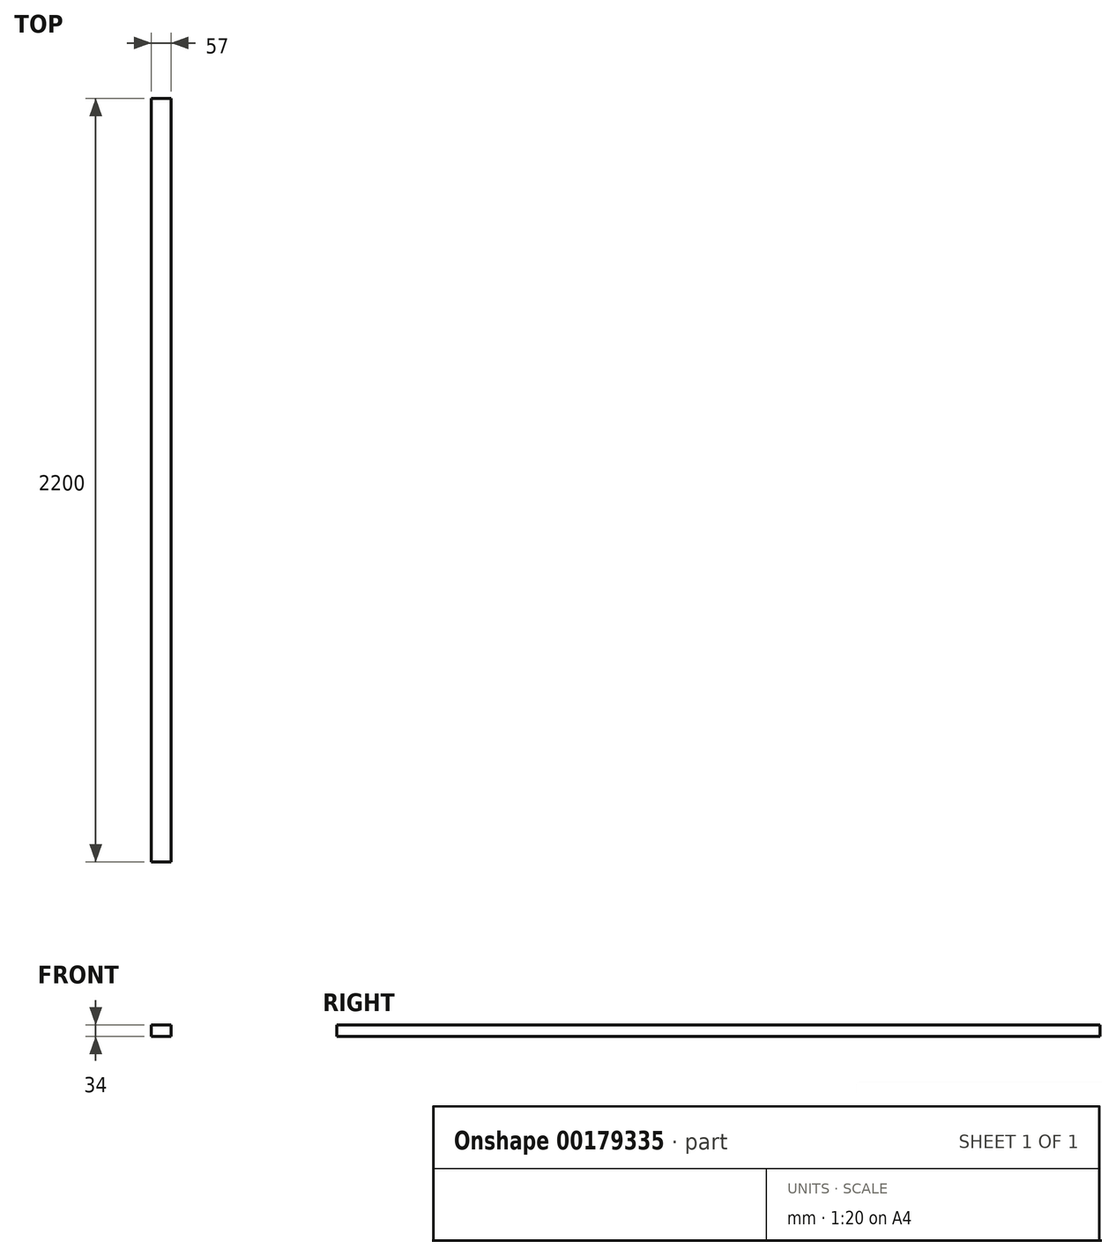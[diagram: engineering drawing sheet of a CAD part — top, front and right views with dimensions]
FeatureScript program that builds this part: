
annotation { "Feature Type Name" : "Feature", "Feature Type Description" : "" }
export const myFeature = defineFeature(function(context is Context, id is Id, definition is map)
    precondition{}
    {
        {
            var Q0;
            Q0=qCreatedBy(makeId("Front.planeOp"),FACE);
            var sketch = newSketch(context, id + "F0", { "sketchPlane" : qUnion([Q0])});
            skLineSegment(sketch, "E0.bottom", {"start": v(28.5, 17) * mm, "end": v(-28.5, 17) * mm});
            skLineSegment(sketch, "E0.top", {"start": v(28.5, -17) * mm, "end": v(-28.5, -17) * mm});
            skLineSegment(sketch, "E0.left", {"start": v(28.5, 17) * mm, "end": v(28.5, -17) * mm});
            skLineSegment(sketch, "E0.right", {"start": v(-28.5, 17) * mm, "end": v(-28.5, -17) * mm});
            skPoint(sketch, "E0.middle", {"position": v(0, 0) * mm});
            skSolve(sketch);
        }
        {
            var Q0;
            Q0=makeQuery(id+"F0.imprint","IMPRINT",FACE,{"disambiguationData":[TD([[makeQuery(id+"F0.imprint","IMPRINT",EDGE,{"derivedFrom":sQuery(id+"F0.wireOp",EDGE,"E0.bottom")}),1.0]])]});
            extrude(context, id + "F1", {"entities" : qUnion([Q0]), "depth" : 2200 * mm});
        }
    });
